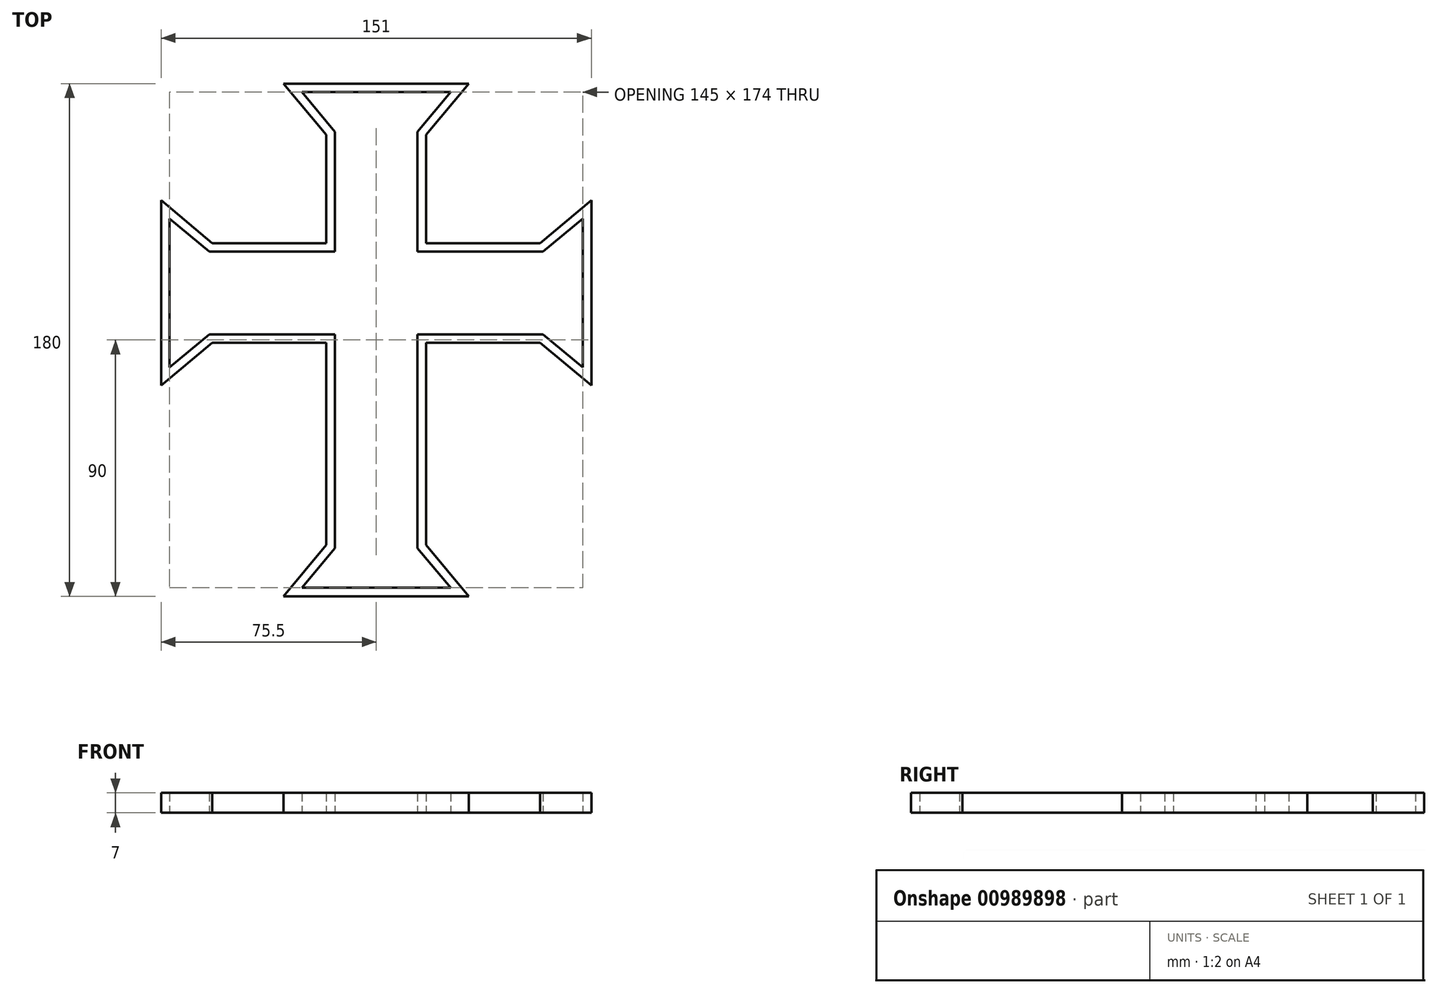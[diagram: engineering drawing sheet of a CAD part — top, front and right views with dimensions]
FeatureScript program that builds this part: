
annotation { "Feature Type Name" : "Feature", "Feature Type Description" : "" }
export const myFeature = defineFeature(function(context is Context, id is Id, definition is map)
    precondition{}
    {
        {
            var Q0;
            Q0=qCreatedBy(makeId("Top.planeOp"),FACE);
            var sketch = newSketch(context, id + "F0", { "sketchPlane" : qUnion([Q0])});
            skLineSegment(sketch, "E0", {"start": v(-17.5, 0) * mm, "end": v(-17.5, -38) * mm});
            skLineSegment(sketch, "E1", {"start": v(-17.5, -38) * mm, "end": v(-57.5, -38) * mm});
            skLineSegment(sketch, "E2", {"start": v(-57.5, -73) * mm, "end": v(-17.5, -73) * mm});
            skLineSegment(sketch, "E3", {"start": v(-17.5, -73) * mm, "end": v(-17.5, -144) * mm});
            skLineSegment(sketch, "E4", {"start": v(17.5, -144) * mm, "end": v(17.5, -73) * mm});
            skLineSegment(sketch, "E5", {"start": v(17.5, -73) * mm, "end": v(57.5, -73) * mm});
            skLineSegment(sketch, "E6", {"start": v(57.5, -38) * mm, "end": v(17.5, -38) * mm});
            skLineSegment(sketch, "E7", {"start": v(17.5, -38) * mm, "end": v(17.5, 0) * mm});
            skLineSegment(sketch, "E8", {"start": v(32.5, 18) * mm, "end": v(-32.5, 18) * mm});
            skLineSegment(sketch, "E9", {"start": v(-17.5, 0) * mm, "end": v(17.5, 0) * mm, "construction": true});
            skPoint(sketch, "E10", {"position": v(0, 18) * mm});
            skPoint(sketch, "E11", {"position": v(0, 0) * mm});
            skLineSegment(sketch, "E12", {"start": v(-32.5, -162) * mm, "end": v(32.5, -162) * mm});
            skPoint(sketch, "E13", {"position": v(0, -162) * mm});
            skLineSegment(sketch, "E14", {"start": v(57.5, -38) * mm, "end": v(57.5, -73) * mm, "construction": true});
            skLineSegment(sketch, "E15", {"start": v(-57.5, -38) * mm, "end": v(-57.5, -73) * mm, "construction": true});
            skPoint(sketch, "E16", {"position": v(-57.5, -55.5) * mm});
            skPoint(sketch, "E17", {"position": v(57.5, -55.5) * mm});
            skLineSegment(sketch, "E18", {"start": v(75.5, -23) * mm, "end": v(75.5, -88) * mm});
            skLineSegment(sketch, "E19", {"start": v(-75.5, -23) * mm, "end": v(-75.5, -88) * mm});
            skPoint(sketch, "E20", {"position": v(75.5, -55.5) * mm});
            skPoint(sketch, "E21", {"position": v(-75.5, -55.5) * mm});
            skLineSegment(sketch, "E22", {"start": v(-17.5, -144) * mm, "end": v(17.5, -144) * mm, "construction": true});
            skPoint(sketch, "E23", {"position": v(0, -144) * mm});
            skLineSegment(sketch, "E24", {"start": v(-17.5, 0) * mm, "end": v(-32.5, 18) * mm});
            skLineSegment(sketch, "E25", {"start": v(17.5, 0) * mm, "end": v(32.5, 18) * mm});
            skLineSegment(sketch, "E26", {"start": v(57.5, -38) * mm, "end": v(75.5, -23) * mm});
            skLineSegment(sketch, "E27", {"start": v(57.5, -73) * mm, "end": v(75.5, -88) * mm});
            skLineSegment(sketch, "E28", {"start": v(-17.5, -144) * mm, "end": v(-32.5, -162) * mm});
            skLineSegment(sketch, "E29", {"start": v(17.5, -144) * mm, "end": v(32.5, -162) * mm});
            skLineSegment(sketch, "E30", {"start": v(-57.5, -38) * mm, "end": v(-75.5, -23) * mm});
            skLineSegment(sketch, "E31", {"start": v(-57.5, -73) * mm, "end": v(-75.5, -88) * mm});
            skSolve(sketch);
        }
        {
            var Q0;
            Q0 = qSketchRegion(id + "F0", true);
            extrude(context, id + "F1", {"entities" : qUnion([Q0]), "depth" : 7 * mm, "offsetDistance" : 25 * mm});
        }
        {
            var Q0;
            Q0=makeQuery(id+"F1.opExtrude","CAP_FACE",FACE,{"disambiguationData":[OSD([sQuery(id+"F0.wireOp",EDGE,"E0"),sQuery(id+"F0.wireOp",EDGE,"E1"),sQuery(id+"F0.wireOp",EDGE,"E2"),sQuery(id+"F0.wireOp",EDGE,"E3"),sQuery(id+"F0.wireOp",EDGE,"E4"),sQuery(id+"F0.wireOp",EDGE,"E5"),sQuery(id+"F0.wireOp",EDGE,"E6"),sQuery(id+"F0.wireOp",EDGE,"E7"),sQuery(id+"F0.wireOp",EDGE,"E8"),sQuery(id+"F0.wireOp",EDGE,"E12"),sQuery(id+"F0.wireOp",EDGE,"E18"),sQuery(id+"F0.wireOp",EDGE,"E19"),sQuery(id+"F0.wireOp",EDGE,"E24"),sQuery(id+"F0.wireOp",EDGE,"E25"),sQuery(id+"F0.wireOp",EDGE,"E26"),sQuery(id+"F0.wireOp",EDGE,"E27"),sQuery(id+"F0.wireOp",EDGE,"E28"),sQuery(id+"F0.wireOp",EDGE,"E29"),sQuery(id+"F0.wireOp",EDGE,"E30"),sQuery(id+"F0.wireOp",EDGE,"E31")])],"isStart":false});
            shell(context, id + "F2", {"entities" : qUnion([Q0]), "thickness" : 3 * mm});
        }
        {
            var Q0;
            Q0=makeQuery(id+"F2.opShell","OFFSET_FACE",FACE,{"disambiguationData":[OSD([sQuery(id+"F0.wireOp",EDGE,"E0"),sQuery(id+"F0.wireOp",EDGE,"E1"),sQuery(id+"F0.wireOp",EDGE,"E2"),sQuery(id+"F0.wireOp",EDGE,"E3"),sQuery(id+"F0.wireOp",EDGE,"E4"),sQuery(id+"F0.wireOp",EDGE,"E5"),sQuery(id+"F0.wireOp",EDGE,"E6"),sQuery(id+"F0.wireOp",EDGE,"E7"),sQuery(id+"F0.wireOp",EDGE,"E8"),sQuery(id+"F0.wireOp",EDGE,"E12"),sQuery(id+"F0.wireOp",EDGE,"E18"),sQuery(id+"F0.wireOp",EDGE,"E19"),sQuery(id+"F0.wireOp",EDGE,"E24"),sQuery(id+"F0.wireOp",EDGE,"E25"),sQuery(id+"F0.wireOp",EDGE,"E26"),sQuery(id+"F0.wireOp",EDGE,"E27"),sQuery(id+"F0.wireOp",EDGE,"E28"),sQuery(id+"F0.wireOp",EDGE,"E29"),sQuery(id+"F0.wireOp",EDGE,"E30"),sQuery(id+"F0.wireOp",EDGE,"E31")])]});
            extrude(context, id + "F3", {"entities" : qUnion([Q0]), "operationType" : NewBodyOperationType.REMOVE, "oppositeDirection" : true, "depth" : 25 * mm, "offsetDistance" : 25 * mm});
        }
    });
